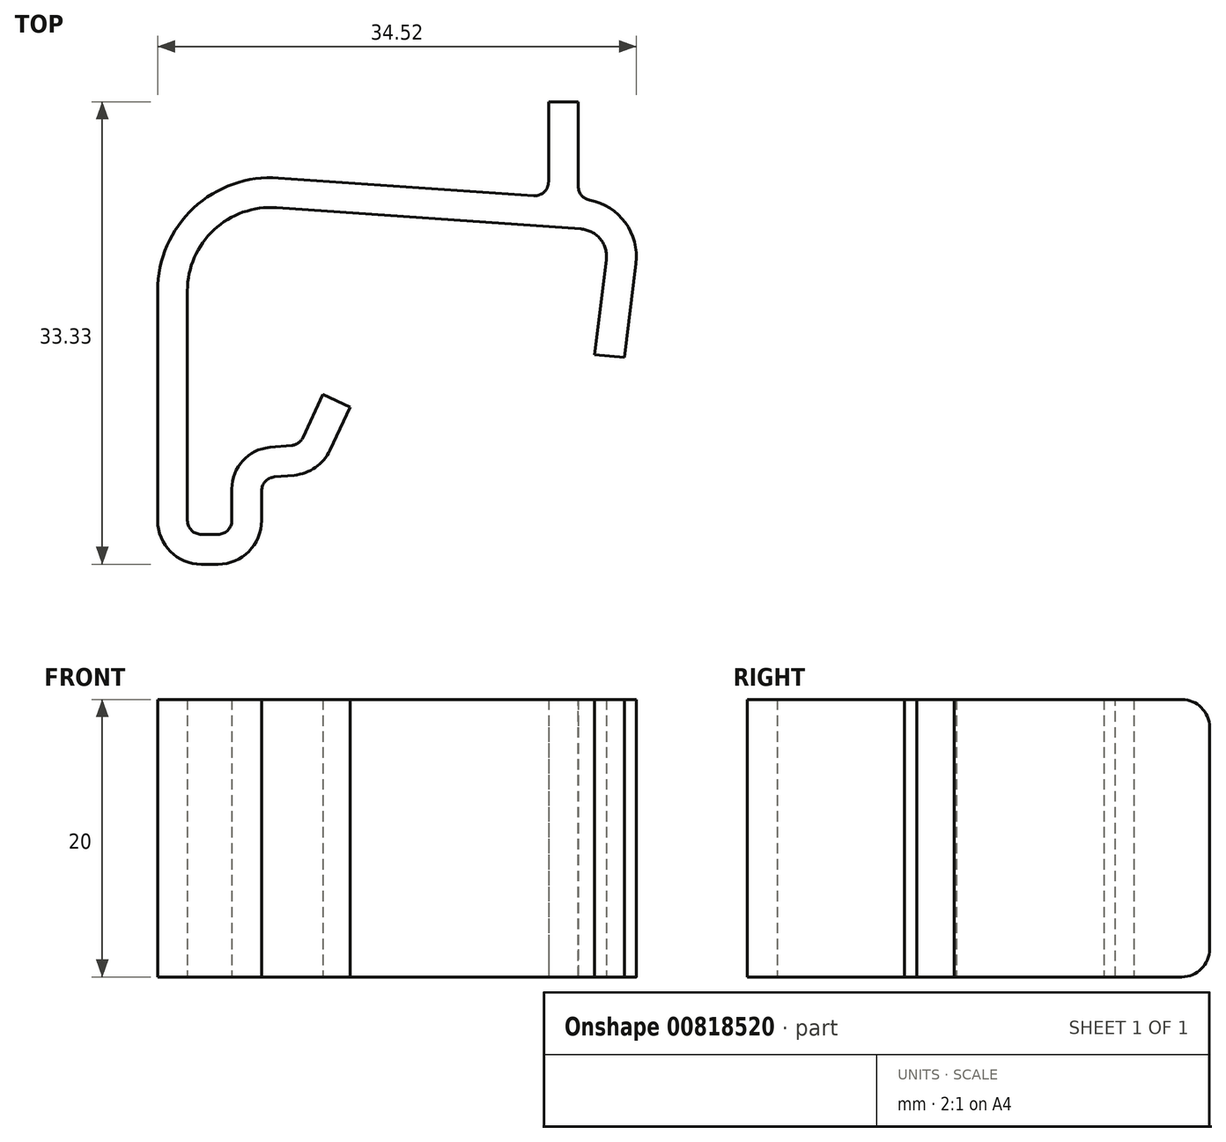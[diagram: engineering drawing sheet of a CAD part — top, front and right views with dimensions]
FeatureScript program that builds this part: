
annotation { "Feature Type Name" : "Feature", "Feature Type Description" : "" }
export const myFeature = defineFeature(function(context is Context, id is Id, definition is map)
    precondition{}
    {
        {
            var Q0;
            Q0=qCreatedBy(makeId("Top.planeOp"),FACE);
            var sketch = newSketch(context, id + "F0", { "sketchPlane" : qUnion([Q0])});
            skLineSegment(sketch, "E0", {"start": v(0, 1) * mm, "end": v(0, 17.57) * mm});
            skLineSegment(sketch, "E1", {"start": v(6.42, 23.55) * mm, "end": v(28.36, 22.02) * mm});
            skLineSegment(sketch, "E2", {"start": v(30.2, 19.78) * mm, "end": v(29.37, 12.94) * mm});
            skLineSegment(sketch, "E3", {"start": v(1, 0) * mm, "end": v(2.2, 0) * mm});
            skLineSegment(sketch, "E4", {"start": v(3.2, 1) * mm, "end": v(3.2, 3.28) * mm});
            skLineSegment(sketch, "E5", {"start": v(5.94, 6.27) * mm, "end": v(7.5, 6.4) * mm});
            skLineSegment(sketch, "E6", {"start": v(8.33, 6.98) * mm, "end": v(9.77, 10.08) * mm});
            skLineSegment(sketch, "E7", {"start": v(9.77, 10.08) * mm, "end": v(11.72, 9.17) * mm});
            skLineSegment(sketch, "E8", {"start": v(32.3, 6.03) * mm, "end": v(-18.06, 6.03) * mm, "construction": true});
            skLineSegment(sketch, "E9.0", {"start": v(32.34, 19.52) * mm, "end": v(31.51, 12.76) * mm});
            skLineSegment(sketch, "E9.1", {"start": v(6.57, 25.7) * mm, "end": v(28.51, 24.16) * mm});
            skLineSegment(sketch, "E9.2", {"start": v(-2.15, 1) * mm, "end": v(-2.15, 17.57) * mm});
            skLineSegment(sketch, "E9.3", {"start": v(1, -2.15) * mm, "end": v(2.2, -2.15) * mm});
            skLineSegment(sketch, "E9.5", {"start": v(10.27, 6.07) * mm, "end": v(11.72, 9.17) * mm});
            skLineSegment(sketch, "E9.6", {"start": v(6.26, 4.14) * mm, "end": v(7.7, 4.27) * mm});
            skLineSegment(sketch, "E9.7", {"start": v(5.35, 1) * mm, "end": v(5.35, 3.14) * mm});
            skLineSegment(sketch, "E10", {"start": v(29.37, 12.94) * mm, "end": v(31.51, 12.76) * mm});
            skPoint(sketch, "E11.visualSharp", {"position": v(0, 24) * mm});
            skArc(sketch, "E11.filletArc", {"start": v(6.42, 23.55) * mm, "mid": v(1.9, 21.95) * mm, "end": v(0, 17.57) * mm});
            skPoint(sketch, "E12.visualSharp", {"position": v(-2.15, 26.3) * mm});
            skArc(sketch, "E12.filletArc", {"start": v(6.57, 25.7) * mm, "mid": v(0.44, 23.53) * mm, "end": v(-2.15, 17.57) * mm});
            skPoint(sketch, "E13.visualSharp", {"position": v(30.47, 21.87) * mm});
            skArc(sketch, "E13.filletArc", {"start": v(30.2, 19.78) * mm, "mid": v(29.77, 21.3) * mm, "end": v(28.36, 22.02) * mm});
            skPoint(sketch, "E14.visualSharp", {"position": v(32.88, 23.86) * mm});
            skArc(sketch, "E14.filletArc", {"start": v(32.34, 19.52) * mm, "mid": v(31.43, 22.66) * mm, "end": v(28.51, 24.16) * mm});
            skPoint(sketch, "E15.visualSharp", {"position": v(0, 0) * mm});
            skArc(sketch, "E15.filletArc", {"start": v(0, 1) * mm, "mid": v(0.3, 0.3) * mm, "end": v(1, 0) * mm});
            skPoint(sketch, "E16.visualSharp", {"position": v(3.2, 0) * mm});
            skArc(sketch, "E16.filletArc", {"start": v(2.2, 0) * mm, "mid": v(2.9, 0.3) * mm, "end": v(3.2, 1) * mm});
            skPoint(sketch, "E17.visualSharp", {"position": v(-2.15, -2.15) * mm});
            skArc(sketch, "E17.filletArc", {"start": v(-2.15, 1) * mm, "mid": v(-1.23, -1.23) * mm, "end": v(1, -2.15) * mm});
            skPoint(sketch, "E18.visualSharp", {"position": v(5.35, -2.15) * mm});
            skArc(sketch, "E18.filletArc", {"start": v(2.2, -2.15) * mm, "mid": v(4.43, -1.23) * mm, "end": v(5.35, 1) * mm});
            skPoint(sketch, "E19.visualSharp", {"position": v(3.2, 6.03) * mm});
            skArc(sketch, "E19.filletArc", {"start": v(5.94, 6.27) * mm, "mid": v(3.99, 5.3) * mm, "end": v(3.2, 3.28) * mm});
            skPoint(sketch, "E20.visualSharp", {"position": v(5.35, 4.06) * mm});
            skArc(sketch, "E20.filletArc", {"start": v(6.26, 4.14) * mm, "mid": v(5.61, 3.82) * mm, "end": v(5.35, 3.14) * mm});
            skPoint(sketch, "E21.visualSharp", {"position": v(8.08, 6.46) * mm});
            skArc(sketch, "E21.filletArc", {"start": v(7.5, 6.4) * mm, "mid": v(8, 6.58) * mm, "end": v(8.33, 6.98) * mm});
            skPoint(sketch, "E22.visualSharp", {"position": v(9.5, 4.42) * mm});
            skArc(sketch, "E22.filletArc", {"start": v(7.7, 4.27) * mm, "mid": v(9.23, 4.82) * mm, "end": v(10.27, 6.07) * mm});
            skLineSegment(sketch, "E23.bottom", {"start": v(28.19, 24.18) * mm, "end": v(26.04, 24.18) * mm});
            skLineSegment(sketch, "E23.top", {"start": v(28.19, 31.18) * mm, "end": v(26.04, 31.18) * mm});
            skLineSegment(sketch, "E23.left", {"start": v(28.19, 24.18) * mm, "end": v(28.19, 31.18) * mm});
            skLineSegment(sketch, "E23.right", {"start": v(26.04, 24.18) * mm, "end": v(26.04, 31.18) * mm});
            skSolve(sketch);
        }
        {
            var Q0;
            Q0=qSketchRegion(id+"F0",true);
            extrude(context, id + "F1", {"entities" : qUnion([Q0]), "depth" : 20 * mm, "offsetDistance" : 25 * mm});
        }
        {
            var Q0;
            Q0=makeQuery(id+"F1.opExtrude","CAP_EDGE",EDGE,{"disambiguationData":[OSD([sQuery(id+"F0.wireOp",EDGE,"E23.top")])],"isStart":false});
            var Q1;
            Q1=makeQuery(id+"F1.opExtrude","CAP_EDGE",EDGE,{"disambiguationData":[OSD([sQuery(id+"F0.wireOp",EDGE,"E23.top")])],"isStart":true});
            fillet(context, id + "F2", {"entities" : qUnion([Q0, Q1]), "radius" : 2 * mm, "tangentPropagation" : true, "allowEdgeOverflow" : false});
        }
        {
            var Q0;
            Q0=makeQuery(id+"F1.opExtrude","SWEPT_EDGE",EDGE,{"disambiguationData":[OSD([sQuery(id+"F0.wireOp",EDGE,"E9.1"),sQuery(id+"F0.wireOp",EDGE,"E23.right")])]});
            var Q1;
            Q1=makeQuery(id+"F1.opExtrude","SWEPT_EDGE",EDGE,{"disambiguationData":[OSD([sQuery(id+"F0.wireOp",EDGE,"E9.1"),sQuery(id+"F0.wireOp",EDGE,"E23.bottom"),sQuery(id+"F0.wireOp",EDGE,"E23.left")])]});
            fillet(context, id + "F3", {"entities" : qUnion([Q0, Q1]), "radius" : 1 * mm, "tangentPropagation" : true, "allowEdgeOverflow" : false});
        }
    });
